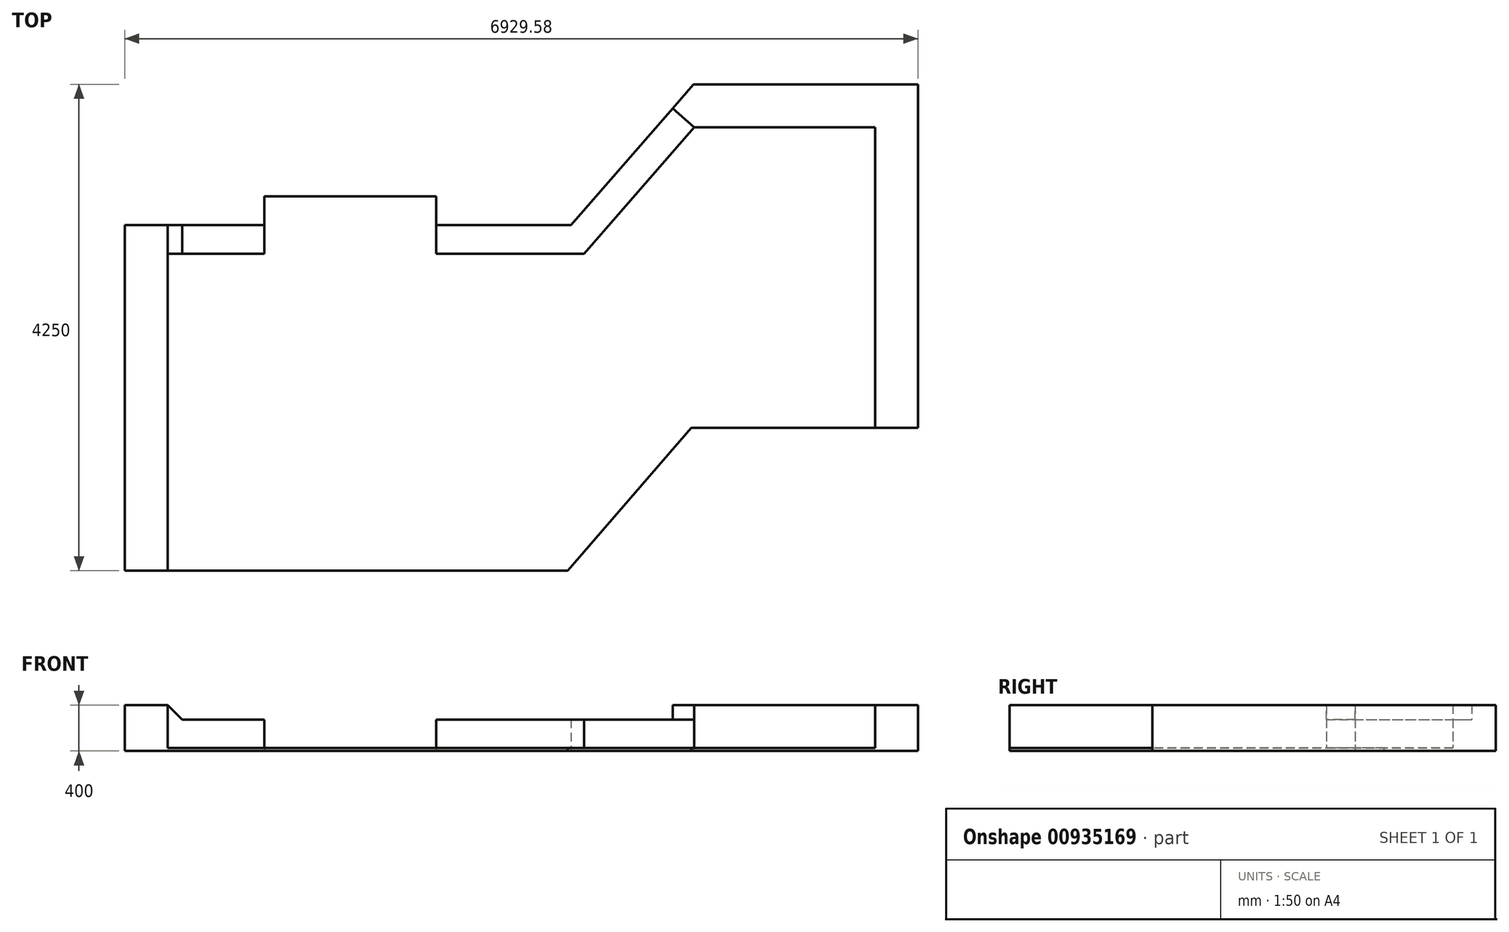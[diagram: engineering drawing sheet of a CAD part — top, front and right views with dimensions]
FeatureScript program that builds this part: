
annotation { "Feature Type Name" : "Feature", "Feature Type Description" : "" }
export const myFeature = defineFeature(function(context is Context, id is Id, definition is map)
    precondition{}
    {
        {
            var Q0;
            Q0=qCreatedBy(makeId("Top.planeOp"),FACE);
            var sketch = newSketch(context, id + "F0", { "sketchPlane" : qUnion([Q0])});
            skLineSegment(sketch, "E0", {"start": v(-949.42, 0) * mm, "end": v(-4820, 0) * mm});
            skLineSegment(sketch, "E1", {"start": v(-4820, 0) * mm, "end": v(-4820, 3020) * mm});
            skLineSegment(sketch, "E2", {"start": v(-4820, 3020) * mm, "end": v(-3600, 3020) * mm});
            skLineSegment(sketch, "E3", {"start": v(-3600, 3020) * mm, "end": v(-3600, 3270) * mm});
            skLineSegment(sketch, "E4", {"start": v(-3600, 3270) * mm, "end": v(-2100, 3270) * mm});
            skLineSegment(sketch, "E5", {"start": v(-2100, 3270) * mm, "end": v(-2100, 3020) * mm});
            skLineSegment(sketch, "E6", {"start": v(-2100, 3020) * mm, "end": v(-920, 3020) * mm});
            skLineSegment(sketch, "E7", {"start": v(-920, 3020) * mm, "end": v(149.58, 4250) * mm});
            skLineSegment(sketch, "E8", {"start": v(149.58, 4250) * mm, "end": v(2109.58, 4250) * mm});
            skLineSegment(sketch, "E9", {"start": v(2109.58, 4250) * mm, "end": v(2109.58, 1250) * mm});
            skLineSegment(sketch, "E10", {"start": v(2109.58, 1250) * mm, "end": v(129.58, 1250) * mm});
            skLineSegment(sketch, "E11", {"start": v(129.58, 1250) * mm, "end": v(-949.42, 0) * mm});
            skSolve(sketch);
        }
        {
            var Q0;
            Q0 = qSketchRegion(id + "F0", true);
            extrude(context, id + "F1", {"entities" : qUnion([Q0]), "depth" : 25 * mm, "offsetDistance" : 25 * mm});
        }
        {
            var Q0;
            Q0=makeQuery(id+"F1.opExtrude","CAP_FACE",FACE,{"disambiguationData":[OSD([sQuery(id+"F0.wireOp",EDGE,"E0"),sQuery(id+"F0.wireOp",EDGE,"E1"),sQuery(id+"F0.wireOp",EDGE,"E2"),sQuery(id+"F0.wireOp",EDGE,"E3"),sQuery(id+"F0.wireOp",EDGE,"E4"),sQuery(id+"F0.wireOp",EDGE,"E5"),sQuery(id+"F0.wireOp",EDGE,"E6"),sQuery(id+"F0.wireOp",EDGE,"E7"),sQuery(id+"F0.wireOp",EDGE,"E8"),sQuery(id+"F0.wireOp",EDGE,"E9"),sQuery(id+"F0.wireOp",EDGE,"E10"),sQuery(id+"F0.wireOp",EDGE,"E11")])],"isStart":false});
            var sketch = newSketch(context, id + "F2", { "sketchPlane" : qUnion([Q0])});
            skLineSegment(sketch, "E12.0", {"start": v(1984.58, 4125) * mm, "end": v(1984.58, 1250) * mm});
            skLineSegment(sketch, "E12.1", {"start": v(206.53, 4125) * mm, "end": v(1984.58, 4125) * mm});
            skLineSegment(sketch, "E12.2", {"start": v(-863.05, 2895) * mm, "end": v(206.53, 4125) * mm});
            skLineSegment(sketch, "E12.3", {"start": v(-2100, 2895) * mm, "end": v(-863.05, 2895) * mm});
            skLineSegment(sketch, "E12.5", {"start": v(-4695, 0) * mm, "end": v(-4695, 2895) * mm});
            skLineSegment(sketch, "E12.6", {"start": v(-4695, 2895) * mm, "end": v(-3600, 2895) * mm});
            skLineSegment(sketch, "E13.0", {"start": v(1859.58, 4000) * mm, "end": v(1859.58, 1250) * mm});
            skLineSegment(sketch, "E13.1", {"start": v(263.49, 4000) * mm, "end": v(1859.58, 4000) * mm});
            skLineSegment(sketch, "E13.2", {"start": v(-806.1, 2770) * mm, "end": v(263.49, 4000) * mm});
            skLineSegment(sketch, "E13.3", {"start": v(-2100, 2770) * mm, "end": v(-806.1, 2770) * mm});
            skLineSegment(sketch, "E13.5", {"start": v(-4570, 0) * mm, "end": v(-4570, 2770) * mm});
            skLineSegment(sketch, "E13.6", {"start": v(-4570, 2770) * mm, "end": v(-3600, 2770) * mm});
            skLineSegment(sketch, "E14.0", {"start": v(1734.58, 3875) * mm, "end": v(1734.58, 1250) * mm});
            skLineSegment(sketch, "E14.1", {"start": v(320.44, 3875) * mm, "end": v(1734.58, 3875) * mm});
            skLineSegment(sketch, "E14.2", {"start": v(-749.14, 2645) * mm, "end": v(320.44, 3875) * mm});
            skLineSegment(sketch, "E14.3", {"start": v(-2100, 2645) * mm, "end": v(-749.14, 2645) * mm});
            skLineSegment(sketch, "E14.5", {"start": v(-4445, 0) * mm, "end": v(-4445, 2645) * mm});
            skLineSegment(sketch, "E14.6", {"start": v(-4445, 2645) * mm, "end": v(-3600, 2645) * mm});
            skLineSegment(sketch, "E15", {"start": v(-3600, 3270) * mm, "end": v(-3600, 2645) * mm});
            skLineSegment(sketch, "E16", {"start": v(-2100, 3270) * mm, "end": v(-2100, 2645) * mm});
            skLineSegment(sketch, "E17.0", {"start": v(-4820, 0) * mm, "end": v(-4820, 3020) * mm});
            skLineSegment(sketch, "E18.0", {"start": v(-4820, 3020) * mm, "end": v(-3600, 3020) * mm});
            skLineSegment(sketch, "E19.0", {"start": v(-2100, 3020) * mm, "end": v(-920, 3020) * mm});
            skLineSegment(sketch, "E20.0", {"start": v(-920, 3020) * mm, "end": v(149.58, 4250) * mm});
            skLineSegment(sketch, "E21.0", {"start": v(149.58, 4250) * mm, "end": v(2109.58, 4250) * mm});
            skLineSegment(sketch, "E22.0", {"start": v(2109.58, 4250) * mm, "end": v(2109.58, 1250) * mm});
            skSolve(sketch);
        }
        {
            var Q0;
            {var subQ9=sQuery(id+"F2.wireOp",EDGE,"E14.0");Q0=makeQuery(id+"F2.imprint","IMPRINT",FACE,{"disambiguationData":[TD([[makeQuery(id+"F2.imprint","IMPRINT",EDGE,{"derivedFrom":subQ9}),-1.0]])]});}
            var sketch = newSketch(context, id + "F3", { "sketchPlane" : qUnion([Q0])});
            skLineSegment(sketch, "E23.0", {"start": v(-4820, 0) * mm, "end": v(-4820, 3020) * mm});
            skLineSegment(sketch, "E24.0", {"start": v(-4820, 3020) * mm, "end": v(-3600, 3020) * mm});
            skLineSegment(sketch, "E25.0", {"start": v(-4445, 0) * mm, "end": v(-4445, 2645) * mm});
            skLineSegment(sketch, "E26.0", {"start": v(-4445, 2645) * mm, "end": v(-3600, 2645) * mm});
            skLineSegment(sketch, "E27.0", {"start": v(-3600, 3020) * mm, "end": v(-3600, 2645) * mm});
            skPoint(sketch, "E28.orphan", {"position": v(-3600, 3270) * mm});
            skLineSegment(sketch, "E29.0", {"start": v(-2100, 3020) * mm, "end": v(-2100, 2645) * mm});
            skLineSegment(sketch, "E30.0", {"start": v(-2100, 3020) * mm, "end": v(-920, 3020) * mm});
            skLineSegment(sketch, "E31.0", {"start": v(-2100, 2645) * mm, "end": v(-749.14, 2645) * mm});
            skLineSegment(sketch, "E32.0", {"start": v(-749.14, 2645) * mm, "end": v(320.44, 3875) * mm});
            skLineSegment(sketch, "E33.0", {"start": v(-920, 3020) * mm, "end": v(149.58, 4250) * mm});
            skLineSegment(sketch, "E34.0", {"start": v(149.58, 4250) * mm, "end": v(2109.58, 4250) * mm});
            skLineSegment(sketch, "E35.0", {"start": v(320.44, 3875) * mm, "end": v(1734.58, 3875) * mm});
            skLineSegment(sketch, "E36.0", {"start": v(1734.58, 3875) * mm, "end": v(1734.58, 1250) * mm});
            skLineSegment(sketch, "E37.0", {"start": v(2109.58, 4250) * mm, "end": v(2109.58, 1250) * mm});
            skLineSegment(sketch, "E38", {"start": v(1734.58, 1250) * mm, "end": v(2109.58, 1250) * mm});
            skLineSegment(sketch, "E39", {"start": v(-4820, 0) * mm, "end": v(-4445, 0) * mm});
            skPoint(sketch, "E40.orphan", {"position": v(-2100, 3270) * mm});
            skSolve(sketch);
        }
        {
            var Q0;
            {var subQ9=sQuery(id+"F2.wireOp",EDGE,"E14.0");Q0=makeQuery(id+"F2.imprint","IMPRINT",FACE,{"disambiguationData":[TD([[makeQuery(id+"F2.imprint","IMPRINT",EDGE,{"derivedFrom":subQ9}),-1.0]])]});}
            var sketch = newSketch(context, id + "F4", { "sketchPlane" : qUnion([Q0])});
            skLineSegment(sketch, "E41.0", {"start": v(-4820, 0) * mm, "end": v(-4820, 3020) * mm});
            skLineSegment(sketch, "E42.0", {"start": v(-4820, 3020) * mm, "end": v(-4445, 3020) * mm});
            skLineSegment(sketch, "E43.0", {"start": v(-4445, 0) * mm, "end": v(-4445, 2645) * mm});
            skLineSegment(sketch, "E44.0", {"start": v(-4445, 2645) * mm, "end": v(-3600, 2645) * mm});
            skLineSegment(sketch, "E45.0", {"start": v(154.79, 4250) * mm, "end": v(2109.58, 4250) * mm});
            skLineSegment(sketch, "E46.0", {"start": v(154.79, 3875) * mm, "end": v(1734.58, 3875) * mm});
            skLineSegment(sketch, "E47.0", {"start": v(1734.58, 3875) * mm, "end": v(1734.58, 1250) * mm});
            skLineSegment(sketch, "E48.0", {"start": v(2109.58, 4250) * mm, "end": v(2109.58, 1250) * mm});
            skLineSegment(sketch, "E49", {"start": v(154.79, 4250) * mm, "end": v(154.79, 3875) * mm, "construction": true});
            skLineSegment(sketch, "E50", {"start": v(1734.58, 1250) * mm, "end": v(2109.58, 1250) * mm});
            skLineSegment(sketch, "E51", {"start": v(-4820, 0) * mm, "end": v(-4445, 0) * mm});
            skPoint(sketch, "E52.orphan", {"position": v(149.58, 4250) * mm});
            skPoint(sketch, "E53.orphan", {"position": v(320.44, 3875) * mm});
            skPoint(sketch, "E54.orphan", {"position": v(-3600, 3020) * mm});
            skPoint(sketch, "E55.orphan", {"position": v(-3600, 2645) * mm});
            skLineSegment(sketch, "E56.0", {"start": v(-4570, 2770) * mm, "end": v(-3600, 2770) * mm, "construction": true});
            skLineSegment(sketch, "E57", {"start": v(-4445, 2645) * mm, "end": v(-4445, 3020) * mm});
            skLineSegment(sketch, "E58.0", {"start": v(-806.1, 2770) * mm, "end": v(263.49, 4000) * mm, "construction": true});
            skLineSegment(sketch, "E59.0", {"start": v(-920, 3020) * mm, "end": v(149.58, 4250) * mm, "construction": true});
            skLineSegment(sketch, "E60", {"start": v(154.79, 3875) * mm, "end": v(-33.86, 4039.05) * mm});
            skLineSegment(sketch, "E61", {"start": v(-33.86, 4039.05) * mm, "end": v(149.58, 4250) * mm});
            skLineSegment(sketch, "E62", {"start": v(149.58, 4250) * mm, "end": v(154.79, 4250) * mm});
            skSolve(sketch);
        }
        {
            var Q0;
            Q0 = qSketchRegion(id + "F4", true);
            extrude(context, id + "F5", {"entities" : qUnion([Q0]), "operationType" : NewBodyOperationType.ADD, "depth" : (125 * 3) * mm, "offsetDistance" : 25 * mm});
        }
        {
            var Q0;
            {var subQ9=sQuery(id+"F2.wireOp",EDGE,"E14.0");Q0=makeQuery(id+"F2.imprint","IMPRINT",FACE,{"disambiguationData":[TD([[makeQuery(id+"F2.imprint","IMPRINT",EDGE,{"derivedFrom":subQ9}),-1.0]])]});}
            var sketch = newSketch(context, id + "F6", { "sketchPlane" : qUnion([Q0])});
            skLineSegment(sketch, "E63.0", {"start": v(-4445, 3020) * mm, "end": v(-3600, 3020) * mm});
            skLineSegment(sketch, "E64.0", {"start": v(-4445, 2770) * mm, "end": v(-3600, 2770) * mm});
            skLineSegment(sketch, "E65.0", {"start": v(-3600, 3020) * mm, "end": v(-3600, 2770) * mm});
            skLineSegment(sketch, "E66.0", {"start": v(-2100, 3020) * mm, "end": v(-2100, 2770) * mm});
            skLineSegment(sketch, "E67.0", {"start": v(-2100, 2770) * mm, "end": v(-806.1, 2770) * mm});
            skLineSegment(sketch, "E68.0", {"start": v(-2100, 3020) * mm, "end": v(-920, 3020) * mm});
            skLineSegment(sketch, "E69.0", {"start": v(-920, 3020) * mm, "end": v(-33.86, 4039.05) * mm});
            skLineSegment(sketch, "E70.0", {"start": v(-806.1, 2770) * mm, "end": v(154.79, 3875) * mm});
            skLineSegment(sketch, "E71.0", {"start": v(154.79, 3875) * mm, "end": v(-33.86, 4039.05) * mm});
            skLineSegment(sketch, "E72.0", {"start": v(-4445, 2770) * mm, "end": v(-4445, 3020) * mm});
            skPoint(sketch, "E73.orphan", {"position": v(-4820, 3020) * mm});
            skPoint(sketch, "E74.orphan", {"position": v(-4570, 2770) * mm});
            skPoint(sketch, "E75.orphan", {"position": v(-3600, 2645) * mm});
            skPoint(sketch, "E76.orphan", {"position": v(-2100, 2645) * mm});
            skPoint(sketch, "E77.orphan", {"position": v(149.58, 4250) * mm});
            skPoint(sketch, "E78.orphan", {"position": v(263.49, 4000) * mm});
            skLineSegment(sketch, "E79.1", {"start": v(-4445, 0) * mm, "end": v(-4445, 3020) * mm, "construction": true});
            skSolve(sketch);
        }
        {
            var Q0;
            Q0 = qSketchRegion(id + "F6", true);
            extrude(context, id + "F7", {"entities" : qUnion([Q0]), "operationType" : NewBodyOperationType.ADD, "depth" : 250 * mm, "offsetDistance" : 25 * mm});
        }
        {
            var Q0;
            Q0=makeQuery(id+"F7.opExtrude","SWEPT_FACE",FACE,{"disambiguationData":[OSD([sQuery(id+"F6.wireOp",EDGE,"E64.0")])]});
            var sketch = newSketch(context, id + "F8", { "sketchPlane" : qUnion([Q0])});
            skLineSegment(sketch, "E80", {"start": v(-4445, 275) * mm, "end": v(-4320, 275) * mm});
            skLineSegment(sketch, "E81", {"start": v(-4320, 275) * mm, "end": v(-4445, 400) * mm});
            skLineSegment(sketch, "E82", {"start": v(-4445, 400) * mm, "end": v(-4445, 275) * mm});
            skSolve(sketch);
        }
        {
            var Q0;
            Q0 = qSketchRegion(id + "F8", true);
            var Q1;
            Q1=makeQuery(id+"F7.boolean.opBoolean","MERGE",FACE,{"derivedFrom":[makeQuery(id+"F5.boolean.opBoolean","MERGE",FACE,{"derivedFrom":[makeQuery(id+"F1.opExtrude","SWEPT_FACE",FACE,{"disambiguationData":[OSD([sQuery(id+"F0.wireOp",EDGE,"E2")])]}),makeQuery(id+"F5.opExtrude","SWEPT_FACE",FACE,{"disambiguationData":[OSD([sQuery(id+"F4.wireOp",EDGE,"E42.0")])]})]}),makeQuery(id+"F7.opExtrude","SWEPT_FACE",FACE,{"disambiguationData":[OSD([sQuery(id+"F6.wireOp",EDGE,"E63.0")])]})]});
            extrude(context, id + "F9", {"entities" : qUnion([Q0]), "operationType" : NewBodyOperationType.ADD, "endBound" : BoundingType.UP_TO_SURFACE, "oppositeDirection" : true, "depth" : 25 * mm, "endBoundEntityFace" : qUnion([Q1]), "offsetDistance" : 25 * mm});
        }
    });
